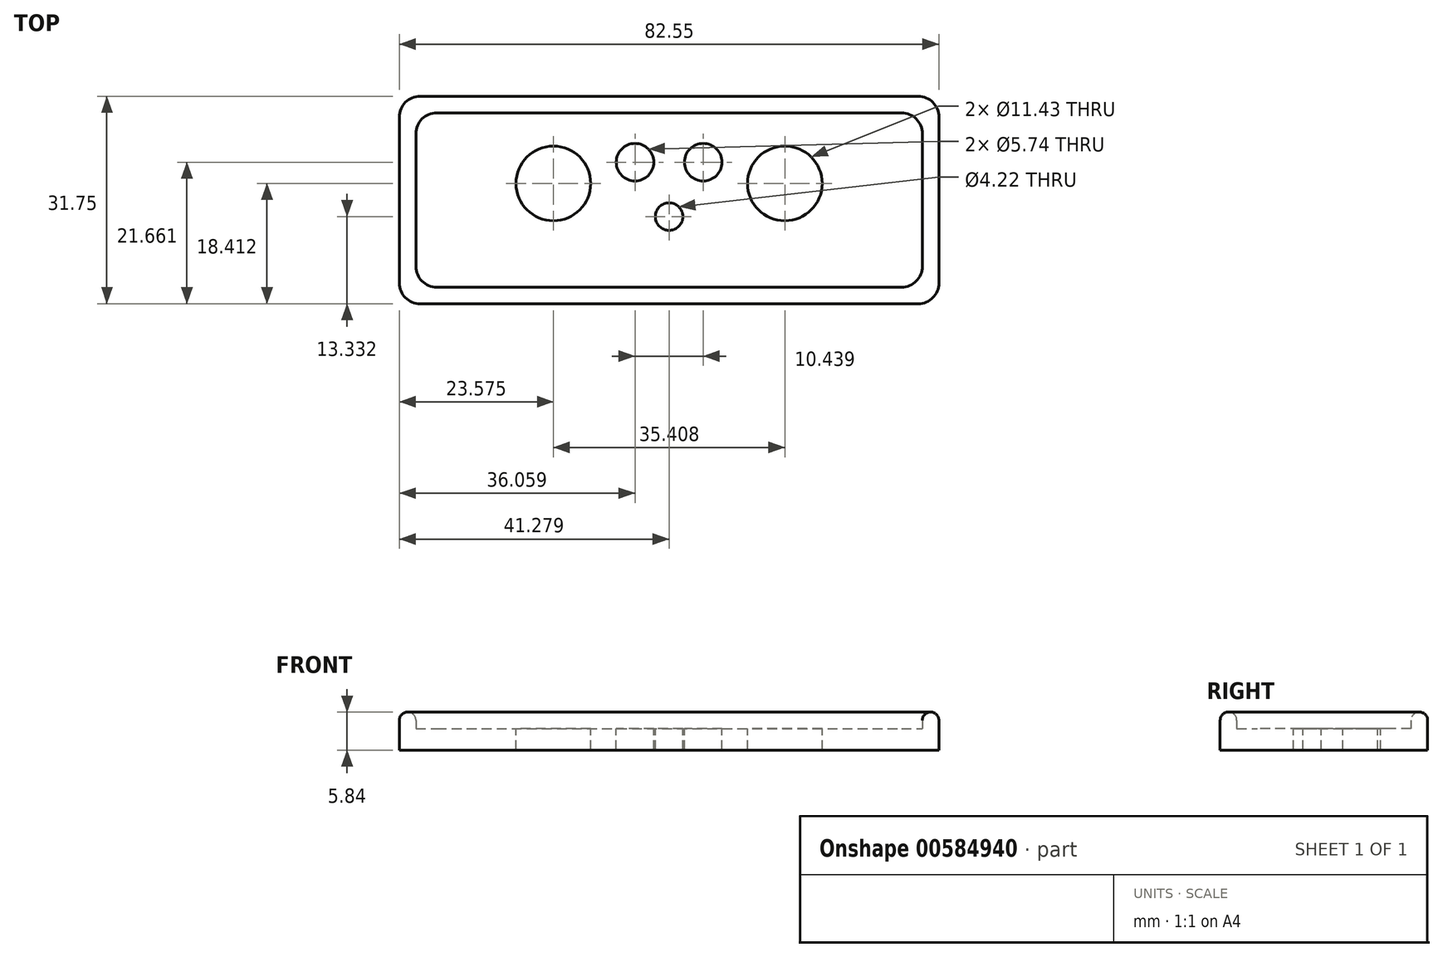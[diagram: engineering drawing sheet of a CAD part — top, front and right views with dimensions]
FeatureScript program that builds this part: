
annotation { "Feature Type Name" : "Feature", "Feature Type Description" : "" }
export const myFeature = defineFeature(function(context is Context, id is Id, definition is map)
    precondition{}
    {
        {
            var Q0;
            Q0=qCreatedBy(makeId("Top.planeOp"),FACE);
            var sketch = newSketch(context, id + "F0", { "sketchPlane" : qUnion([Q0])});
            skLineSegment(sketch, "E0.bottom", {"start": v(12.86, -33.07) * mm, "end": v(83.98, -33.07) * mm});
            skLineSegment(sketch, "E0.top", {"start": v(12.86, -6.4) * mm, "end": v(83.98, -6.4) * mm});
            skLineSegment(sketch, "E0.left", {"start": v(9.68, -9.58) * mm, "end": v(9.68, -29.9) * mm});
            skLineSegment(sketch, "E0.right", {"start": v(87.15, -9.58) * mm, "end": v(87.15, -29.9) * mm});
            skPoint(sketch, "E1", {"position": v(48.42, -6.4) * mm});
            skPoint(sketch, "E2", {"position": v(9.68, -19.74) * mm});
            skLineSegment(sketch, "E3.0", {"start": v(10.32, -3.86) * mm, "end": v(86.52, -3.86) * mm});
            skLineSegment(sketch, "E3.1", {"start": v(7.14, -7.04) * mm, "end": v(7.14, -32.44) * mm});
            skLineSegment(sketch, "E3.2", {"start": v(10.32, -35.61) * mm, "end": v(86.52, -35.61) * mm});
            skLineSegment(sketch, "E3.3", {"start": v(89.7, -7.04) * mm, "end": v(89.7, -32.44) * mm});
            skPoint(sketch, "E4.visualSharp", {"position": v(87.15, -33.07) * mm});
            skArc(sketch, "E4.filletArc", {"start": v(83.98, -33.07) * mm, "mid": v(86.22, -32.14) * mm, "end": v(87.15, -29.9) * mm});
            skPoint(sketch, "E5.visualSharp", {"position": v(87.15, -6.4) * mm});
            skArc(sketch, "E5.filletArc", {"start": v(87.15, -9.58) * mm, "mid": v(86.22, -7.33) * mm, "end": v(83.98, -6.4) * mm});
            skPoint(sketch, "E6.visualSharp", {"position": v(89.7, -35.61) * mm});
            skArc(sketch, "E6.filletArc", {"start": v(86.52, -35.61) * mm, "mid": v(88.76, -34.68) * mm, "end": v(89.7, -32.44) * mm});
            skPoint(sketch, "E7.visualSharp", {"position": v(89.7, -3.86) * mm});
            skArc(sketch, "E7.filletArc", {"start": v(89.7, -7.04) * mm, "mid": v(88.76, -4.8) * mm, "end": v(86.52, -3.86) * mm});
            skPoint(sketch, "E8.visualSharp", {"position": v(9.68, -33.07) * mm});
            skArc(sketch, "E8.filletArc", {"start": v(9.68, -29.9) * mm, "mid": v(10.61, -32.14) * mm, "end": v(12.86, -33.07) * mm});
            skPoint(sketch, "E9.visualSharp", {"position": v(7.14, -35.61) * mm});
            skArc(sketch, "E9.filletArc", {"start": v(7.14, -32.44) * mm, "mid": v(8.07, -34.68) * mm, "end": v(10.32, -35.61) * mm});
            skPoint(sketch, "E10.visualSharp", {"position": v(7.14, -3.86) * mm});
            skArc(sketch, "E10.filletArc", {"start": v(10.32, -3.86) * mm, "mid": v(8.07, -4.8) * mm, "end": v(7.14, -7.04) * mm});
            skPoint(sketch, "E11.visualSharp", {"position": v(9.68, -6.4) * mm});
            skArc(sketch, "E11.filletArc", {"start": v(12.86, -6.4) * mm, "mid": v(10.61, -7.33) * mm, "end": v(9.68, -9.58) * mm});
            skSolve(sketch);
        }
        {
            var Q0;
            Q0=makeQuery(id+"F0.imprint","IMPRINT",FACE,{"disambiguationData":[TD([[makeQuery(id+"F0.imprint","IMPRINT",EDGE,{"derivedFrom":sQuery(id+"F0.wireOp",EDGE,"E0.bottom")}),-1.0]])]});
            var Q1;
            Q1=makeQuery(id+"F0.imprint","IMPRINT",FACE,{"disambiguationData":[TD([[makeQuery(id+"F0.imprint","IMPRINT",EDGE,{"derivedFrom":sQuery(id+"F0.wireOp",EDGE,"E0.bottom")}),1.0]])]});
            extrude(context, id + "F1", {"entities" : qUnion([Q0, Q1]), "oppositeDirection" : true, "depth" : 3.3 * mm, "offsetDistance" : 25.4 * mm});
        }
        {
            var Q0;
            Q0=makeQuery(id+"F0.imprint","IMPRINT",FACE,{"disambiguationData":[TD([[makeQuery(id+"F0.imprint","IMPRINT",EDGE,{"derivedFrom":sQuery(id+"F0.wireOp",EDGE,"E0.bottom")}),-1.0]])]});
            extrude(context, id + "F2", {"entities" : qUnion([Q0]), "operationType" : NewBodyOperationType.ADD, "depth" : 2.54 * mm, "offsetDistance" : 25.4 * mm});
        }
        {
            var Q0;
            Q0=qCreatedBy(makeId("Top.planeOp"),FACE);
            var sketch = newSketch(context, id + "F3", { "sketchPlane" : qUnion([Q0])});
            skCircle(sketch, "E12", {"center": v(30.72, -17.2) * mm, "radius": 5.72 * mm});
            skCircle(sketch, "E13", {"center": v(66.12, -17.2) * mm, "radius": 5.72 * mm});
            skCircle(sketch, "E14", {"center": v(43.2, -13.95) * mm, "radius": 2.87 * mm});
            skCircle(sketch, "E15", {"center": v(53.64, -13.95) * mm, "radius": 2.87 * mm});
            skLineSegment(sketch, "E16", {"start": v(43.2, -13.95) * mm, "end": v(53.64, -13.95) * mm});
            skPoint(sketch, "E17", {"position": v(48.42, -13.95) * mm});
            skLineSegment(sketch, "E18", {"start": v(30.72, -17.2) * mm, "end": v(66.12, -17.2) * mm});
            skPoint(sketch, "E19", {"position": v(48.42, -17.2) * mm});
            skCircle(sketch, "E20", {"center": v(48.42, -22.28) * mm, "radius": 2.11 * mm});
            skSolve(sketch);
        }
        {
            var Q0;
            Q0=qSketchRegion(id+"F3",true);
            extrude(context, id + "F4", {"entities" : qUnion([Q0]), "operationType" : NewBodyOperationType.REMOVE, "endBound" : BoundingType.THROUGH_ALL, "oppositeDirection" : true, "depth" : 25.4 * mm, "offsetDistance" : 25.4 * mm});
        }
        {
            var Q0;
            Q0=makeQuery(id+"F2.opExtrude","CAP_EDGE",EDGE,{"disambiguationData":[OSD([sQuery(id+"F0.wireOp",EDGE,"E0.top")])],"isStart":false});
            var Q1;
            Q1=makeQuery(id+"F2.opExtrude","CAP_EDGE",EDGE,{"disambiguationData":[OSD([sQuery(id+"F0.wireOp",EDGE,"E11.filletArc")])],"isStart":false});
            var Q2;
            Q2=makeQuery(id+"F2.opExtrude","CAP_EDGE",EDGE,{"disambiguationData":[OSD([sQuery(id+"F0.wireOp",EDGE,"E0.left")])],"isStart":false});
            var Q3;
            Q3=makeQuery(id+"F2.opExtrude","CAP_EDGE",EDGE,{"disambiguationData":[OSD([sQuery(id+"F0.wireOp",EDGE,"E8.filletArc")])],"isStart":false});
            var Q4;
            Q4=makeQuery(id+"F2.opExtrude","CAP_EDGE",EDGE,{"disambiguationData":[OSD([sQuery(id+"F0.wireOp",EDGE,"E0.bottom")])],"isStart":false});
            var Q5;
            Q5=makeQuery(id+"F2.opExtrude","CAP_EDGE",EDGE,{"disambiguationData":[OSD([sQuery(id+"F0.wireOp",EDGE,"E0.right")])],"isStart":false});
            var Q6;
            Q6=makeQuery(id+"F2.opExtrude","CAP_EDGE",EDGE,{"disambiguationData":[OSD([sQuery(id+"F0.wireOp",EDGE,"E5.filletArc")])],"isStart":false});
            var Q7;
            Q7=makeQuery(id+"F2.opExtrude","CAP_EDGE",EDGE,{"disambiguationData":[OSD([sQuery(id+"F0.wireOp",EDGE,"E4.filletArc")])],"isStart":false});
            var Q8;
            Q8=makeQuery(id+"F2.opExtrude","CAP_EDGE",EDGE,{"disambiguationData":[OSD([sQuery(id+"F0.wireOp",EDGE,"E3.1")])],"isStart":false});
            var Q9;
            Q9=makeQuery(id+"F2.opExtrude","CAP_EDGE",EDGE,{"disambiguationData":[OSD([sQuery(id+"F0.wireOp",EDGE,"E10.filletArc")])],"isStart":false});
            fillet(context, id + "F5", {"entities" : qUnion([Q0, Q1, Q2, Q3, Q4, Q5, Q6, Q7, Q8, Q9]), "radius" : 1.27 * mm, "tangentPropagation" : true, "allowEdgeOverflow" : false});
        }
    });
